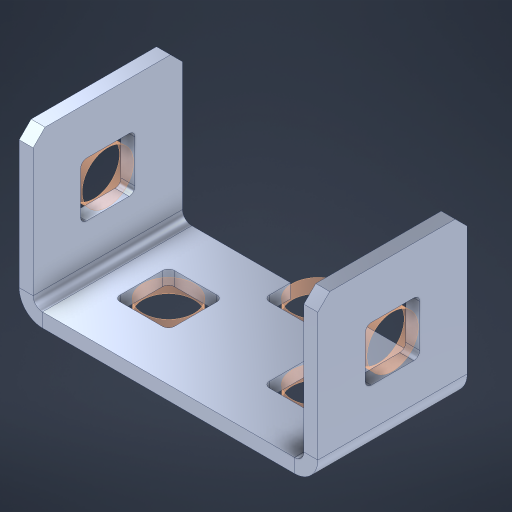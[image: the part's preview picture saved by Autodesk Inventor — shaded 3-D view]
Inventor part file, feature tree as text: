
AUTODESK INVENTOR PART (.ipt)
format: ipt  version: 2023 (Build 270158000, 158)  size: 468,992 bytes
history: native  units: in
note: dims shown in document units (in); Inventor stores cm internally (conversion verified against a paired STEP export)
features: other x45, extrude x36, sheet_metal_op x11, sketch x10, pattern_linear x2, mirror x1, chamfer x1
ambient origin geometry x8: Origin, YZ Plane, XZ Plane, XY Plane, X Axis, Y Axis, Z Axis, Center Point
bodies: Solid1 (feature_tree), Body (feature_tree)
feature tree (106):
  sheet_metal_op  "Flanges"
  other  "Flange Pattern Plane"
  other  "Flange Pattern Sketch"
  sheet_metal_op  "Flange Pattern"
  sheet_metal_op  "Body Pattern"
  pattern_linear  "Center Pattern"  Spacing1=0.0469in  [1 undecoded]
  other  "Arc Length"
  mirror  "Notch Mirror"
  pattern_linear  "Notch Pattern"  Spacing1=0.182in  [1 undecoded]
  chamfer  "End Chamfer"
  extrude  "Half Cut"  Depth=0.02in
  sketch  "Sketch1"  dims[d0=1.0in]
  other  "Plate1"
  sketch  "Sketch2"  dims[d1=0.5in]
  other  "Plate2"
  sheet_metal_op  "Bend1"
  sheet_metal_op  "Corner1"
  sketch  "Sketch3"  dims[d2=0.0469in]
  sketch  "Sketch7"  dims[d3=0.0469in]
  other  "Srf1"
  other  "Srf2"
  sketch  "Sketch8"  dims[d4=0.0234in]
  sketch  "Sketch9"  dims[d5=0.0938in]
  other  "Srf91"
  sheet_metal_op  "Body Pattern Sketch"
  other  "Srf92"
  sketch  "Sketch13"  dims[d6=0.0469in]
  sketch  "Sketch14"  dims[d7=0.5in d8=90.0deg d9=0.0312in]
  sketch  "Sketch15"  dims[d10=0.1875in]
  sketch  "Sketch16"  dims[d11=0.0469in d12=0.0469in d16=0.182in d17=0.02in d18=0.0469in d19=0.0in d20=0.25in d21=0.25in d38=0.3937in d40=0.5in d41=0.7874in d43=1.0in d46=0.172in d47=1.0in d48=0.0in d49=0.182in d50=0.02in d51=0.25in d52=0.25in d53=0.0469in d54=0.0in d55=0.172in d56=1.0in d57=0.0in d58=0.25in d60=0.3937in d62=0.5in d63=0.7874in d65=0.5in d85=0.1227in d86=0.1659in d88=0.04in d89=0.0469in d90=0.0in d91=0.04in d92=0.0491in d95=2.5in d96=0.04in d97=0.25in d98=45.0deg d99=0.25in d100=0.5in d101=0.0in d102=2.497in d106=0.182in d107=0.02in d108=0.5in d109=0.5in d110=0.0469in d111=0.0in d112=0.172in d113=0.5in d114=0.0in d117=0.5in d118=0.5in d119=0.5in]
  other  "Srf786"
  other  "Srf889"
  other  "Srf890"
  other  "Srf891"
  other  "Srf892"
  other  "Srf893"
  other  "Srf894"
  other  "Srf895"
  other  "Srf896"
  other  "Srf996"
  other  "Srf997"
  other  "Srf998"
  other  "Srf999"
  other  "Srf1000"
  other  "Srf1255"
  other  "Srf1256"
  other  "Srf1257"
  other  "Srf1258"
  other  "Srf1259"
  other  "Srf1260"
  other  "Srf1261"
  other  "Srf1262"
  other  "Srf1263"
  other  "Srf1264"
  other  "Srf1265"
  other  "Srf1266"
  other  "Srf1267"
  other  "Srf1268"
  other  "Srf1269"
  other  "Srf1270"
  other  "Srf1271"
  other  "Srf1272"
  other  "Srf1273"
  other  "Srf1274"
  sheet_metal_op  "Flange Stamp"
  sheet_metal_op  "Flange Circle"
  sheet_metal_op  "Body Stamp"
  sheet_metal_op  "Body Circle"
  other  "Center Stamp"
  other  "Center Circle"
  sheet_metal_op  "Notch"
  extrude  "ExtrusionSrf2"  Depth=0.0469in
  extrude  "ExtrusionSrf92"  TaperAngle=0.0deg  [1 undecoded]
  extrude  "ExtrusionSrf889"  Depth=0.25in
  extrude  "ExtrusionSrf890"  Depth=0.25in
  extrude  "ExtrusionSrf891"  Depth=0.3937in
  extrude  "ExtrusionSrf892"  Depth=0.5in
  extrude  "ExtrusionSrf893"  Depth=1.0in TaperAngle=0.0deg
  extrude  "ExtrusionSrf894"  Depth=0.182in
  extrude  "ExtrusionSrf895"  Depth=0.02in
  extrude  "ExtrusionSrf896"  Depth=0.25in
  extrude  "ExtrusionSrf996"  Depth=0.25in
  extrude  "ExtrusionSrf997"  Depth=0.0469in
  extrude  "ExtrusionSrf998"  TaperAngle=0.0deg  [1 undecoded]
  extrude  "ExtrusionSrf999"  Depth=0.5in
  extrude  "ExtrusionSrf1000"  Depth=1.0in TaperAngle=0.0deg
  extrude  "ExtrusionSrf1255"  Depth=0.25in
  extrude  "ExtrusionSrf1256"  Depth=0.3937in
  extrude  "ExtrusionSrf1257"  Depth=0.5in
  extrude  "ExtrusionSrf1258"  Depth=0.5in
  extrude  "ExtrusionSrf1259"  Depth=0.5in
  extrude  "ExtrusionSrf1260"  Depth=0.5in
  extrude  "ExtrusionSrf1261"  Depth=0.0469in
  extrude  "ExtrusionSrf1262"  TaperAngle=0.0deg  [1 undecoded]
  extrude  "ExtrusionSrf1263"  Depth=0.5in
  extrude  "ExtrusionSrf1264"  Depth=0.5in
  extrude  "ExtrusionSrf1265"  Depth=0.5in
  extrude  "ExtrusionSrf1266"  Depth=0.25in TaperAngle=45.0deg
  extrude  "ExtrusionSrf1267"  Depth=0.25in
  extrude  "ExtrusionSrf1268"  Depth=0.5in TaperAngle=0.0deg
  extrude  "ExtrusionSrf1269"  Depth=0.5in
  extrude  "ExtrusionSrf1270"  Depth=0.182in
  extrude  "ExtrusionSrf1271"  Depth=0.02in
  extrude  "ExtrusionSrf1272"  Depth=0.5in
  extrude  "ExtrusionSrf1273"  Depth=0.5in
  extrude  "ExtrusionSrf1274"  Depth=0.0469in
note: 5 required parameter values undecoded (feature->parameter linkage not recoverable at this tier; creation-order binding heuristic only, values carry confidence <= 0.55)
